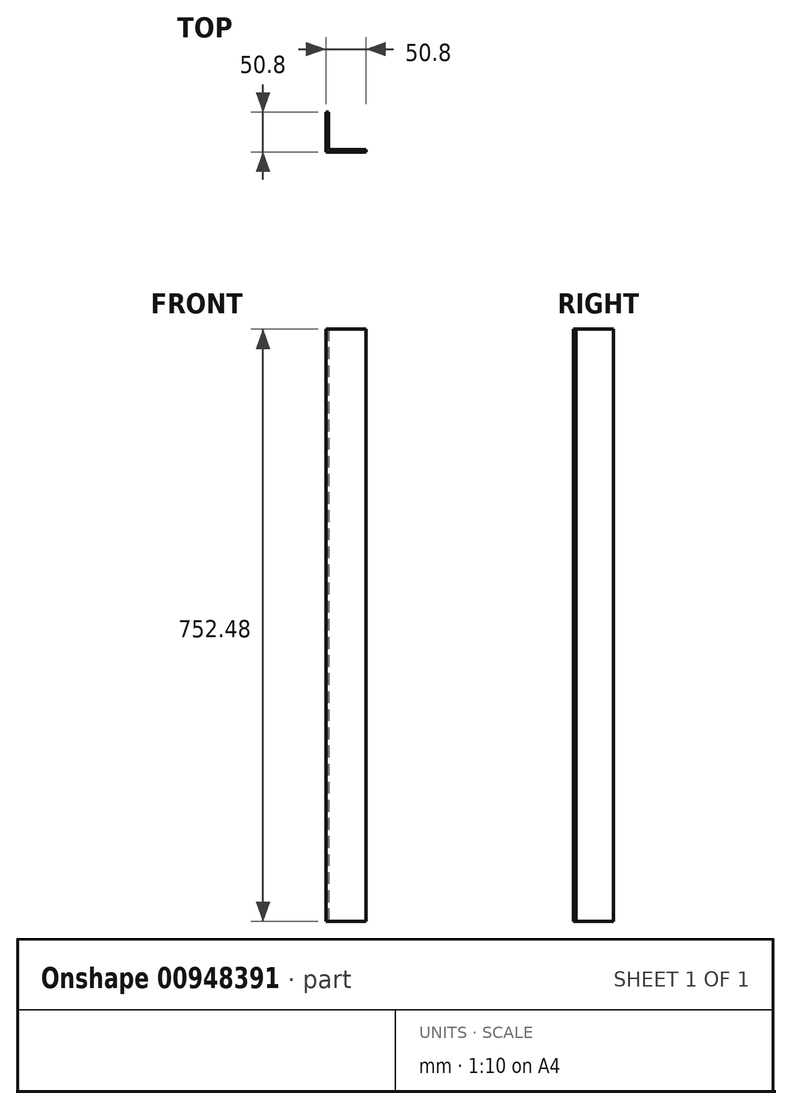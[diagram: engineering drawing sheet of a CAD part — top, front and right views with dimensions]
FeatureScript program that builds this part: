
annotation { "Feature Type Name" : "Feature", "Feature Type Description" : "" }
export const myFeature = defineFeature(function(context is Context, id is Id, definition is map)
    precondition{}
    {
        {
            var Q0;
            Q0=qCreatedBy(makeId("Top.planeOp"),FACE);
            var sketch = newSketch(context, id + "F0", { "sketchPlane" : qUnion([Q0])});
            skLineSegment(sketch, "E0", {"start": v(0, 0) * mm, "end": v(0, 50.8) * mm});
            skLineSegment(sketch, "E1", {"start": v(0, 50.8) * mm, "end": v(3.18, 50.8) * mm});
            skLineSegment(sketch, "E2", {"start": v(3.17, 50.8) * mm, "end": v(3.18, 3.17) * mm});
            skLineSegment(sketch, "E3", {"start": v(3.18, 3.17) * mm, "end": v(50.8, 3.18) * mm});
            skLineSegment(sketch, "E4", {"start": v(50.8, 3.18) * mm, "end": v(50.8, 0) * mm});
            skLineSegment(sketch, "E5", {"start": v(50.8, 0) * mm, "end": v(0, 0) * mm});
            skSolve(sketch);
        }
        {
            var Q0;
            Q0=makeQuery(id+"F0.imprint","IMPRINT",FACE,{"disambiguationData":[TD([[makeQuery(id+"F0.imprint","IMPRINT",EDGE,{"derivedFrom":sQuery(id+"F0.wireOp",EDGE,"E0")}),-1.0]])]});
            extrude(context, id + "F1", {"entities" : qUnion([Q0]), "depth" : 752.47 * mm, "offsetDistance" : 25.4 * mm});
        }
    });
